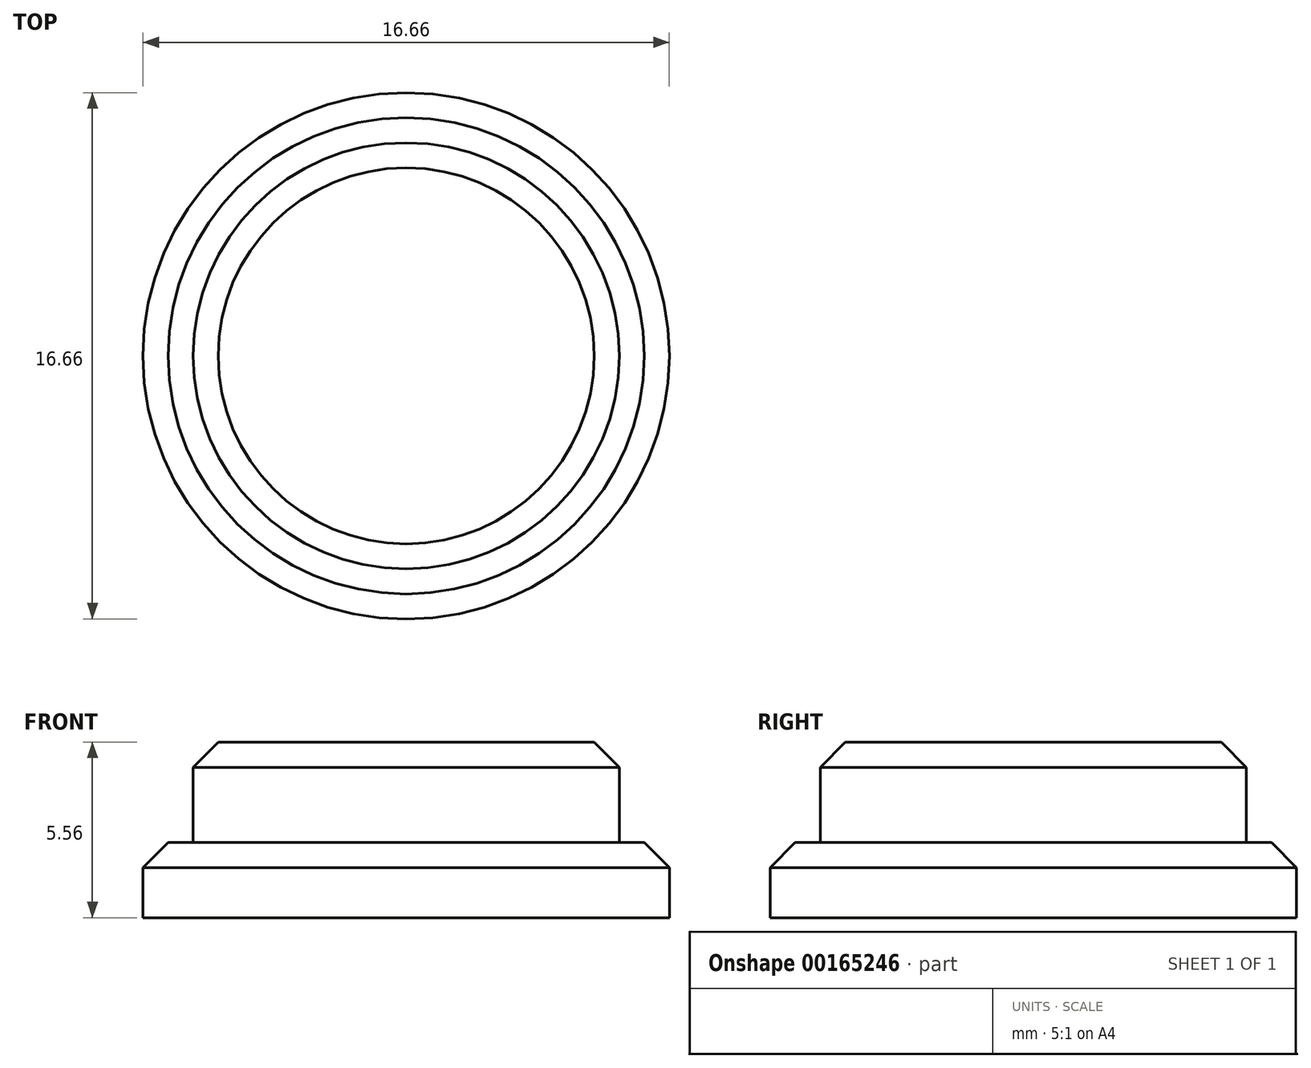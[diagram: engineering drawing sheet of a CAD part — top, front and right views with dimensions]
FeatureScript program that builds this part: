
annotation { "Feature Type Name" : "Feature", "Feature Type Description" : "" }
export const myFeature = defineFeature(function(context is Context, id is Id, definition is map)
    precondition{}
    {
        {
            var Q0;
            Q0=qCreatedBy(makeId("Top.planeOp"),FACE);
            var sketch = newSketch(context, id + "F0", { "sketchPlane" : qUnion([Q0])});
            skCircle(sketch, "E0", {"center": v(0, 0) * mm, "radius": 8.33 * mm});
            skSolve(sketch);
        }
        {
            var Q0;
            Q0 = qSketchRegion(id + "F0", true);
            extrude(context, id + "F1", {"entities" : qUnion([Q0]), "depth" : 2.38 * mm});
        }
        {
            var Q0;
            Q0=makeQuery(id+"F1.opExtrude","CAP_FACE",FACE,{"disambiguationData":[OSD([sQuery(id+"F0.wireOp",EDGE,"E0")])],"isStart":false});
            var sketch = newSketch(context, id + "F2", { "sketchPlane" : qUnion([Q0])});
            skCircle(sketch, "E1", {"center": v(0, 0) * mm, "radius": 6.75 * mm});
            skSolve(sketch);
        }
        {
            var Q0;
            Q0 = qSketchRegion(id + "F2", true);
            extrude(context, id + "F3", {"entities" : qUnion([Q0]), "operationType" : NewBodyOperationType.ADD, "depth" : 3.17 * mm});
        }
        {
            var Q0;
            Q0=makeQuery(id+"F1.opExtrude","CAP_EDGE",EDGE,{"disambiguationData":[OSD([sQuery(id+"F0.wireOp",EDGE,"E0")])],"isStart":false});
            var Q1;
            Q1=makeQuery(id+"F3.opExtrude","CAP_EDGE",EDGE,{"disambiguationData":[OSD([sQuery(id+"F2.wireOp",EDGE,"E1")])],"isStart":false});
            chamfer(context, id + "F4", {"entities" : qUnion([Q0, Q1]), "width" : 0.8 * mm, "tangentPropagation" : true});
        }
    });
